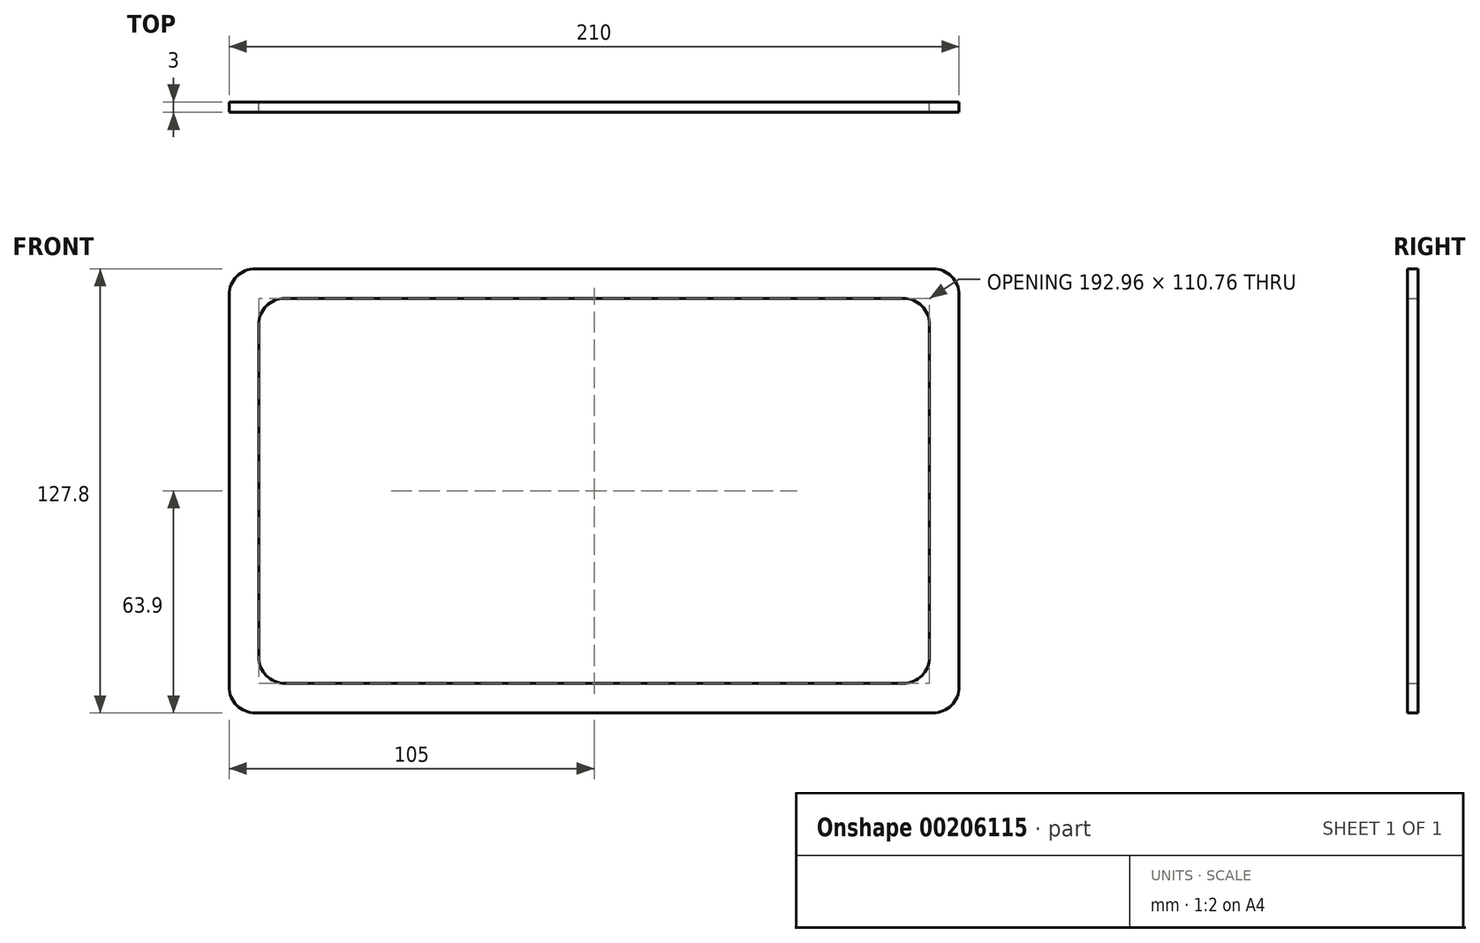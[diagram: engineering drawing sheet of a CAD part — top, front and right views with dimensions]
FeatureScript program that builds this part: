
annotation { "Feature Type Name" : "Feature", "Feature Type Description" : "" }
export const myFeature = defineFeature(function(context is Context, id is Id, definition is map)
    precondition{}
    {
        {
            var Q0;
            Q0=qCreatedBy(makeId("Front.planeOp"),FACE);
            var sketch = newSketch(context, id + "F0", { "sketchPlane" : qUnion([Q0])});
            skLineSegment(sketch, "E0.bottom", {"start": v(96.48, -55.38) * mm, "end": v(-96.48, -55.38) * mm});
            skLineSegment(sketch, "E0.top", {"start": v(96.48, 55.38) * mm, "end": v(-96.48, 55.38) * mm});
            skLineSegment(sketch, "E0.left", {"start": v(96.48, -55.38) * mm, "end": v(96.48, 55.38) * mm});
            skLineSegment(sketch, "E0.right", {"start": v(-96.48, -55.38) * mm, "end": v(-96.48, 55.38) * mm});
            skPoint(sketch, "E0.middle", {"position": v(0, 0) * mm});
            skLineSegment(sketch, "E1.bottom", {"start": v(97.5, 63.9) * mm, "end": v(-97.5, 63.9) * mm});
            skLineSegment(sketch, "E1.top", {"start": v(97.5, -63.9) * mm, "end": v(-97.5, -63.9) * mm});
            skLineSegment(sketch, "E1.left", {"start": v(105, 56.4) * mm, "end": v(105, -56.4) * mm});
            skLineSegment(sketch, "E1.right", {"start": v(-105, 56.4) * mm, "end": v(-105, -56.4) * mm});
            skPoint(sketch, "E2.visualSharp", {"position": v(-105, -63.9) * mm});
            skArc(sketch, "E2.filletArc", {"start": v(-105, -56.4) * mm, "mid": v(-102.8, -61.7) * mm, "end": v(-97.5, -63.9) * mm});
            skPoint(sketch, "E3.visualSharp", {"position": v(105, -63.9) * mm});
            skArc(sketch, "E3.filletArc", {"start": v(97.5, -63.9) * mm, "mid": v(102.8, -61.7) * mm, "end": v(105, -56.4) * mm});
            skPoint(sketch, "E4.visualSharp", {"position": v(105, 63.9) * mm});
            skArc(sketch, "E4.filletArc", {"start": v(105, 56.4) * mm, "mid": v(102.8, 61.7) * mm, "end": v(97.5, 63.9) * mm});
            skPoint(sketch, "E5.visualSharp", {"position": v(-105, 63.9) * mm});
            skArc(sketch, "E5.filletArc", {"start": v(-97.5, 63.9) * mm, "mid": v(-102.8, 61.7) * mm, "end": v(-105, 56.4) * mm});
            skSolve(sketch);
        }
        {
            var Q0;
            Q0=makeQuery(id+"F0.imprint","IMPRINT",FACE,{"disambiguationData":[TD([[makeQuery(id+"F0.imprint","IMPRINT",EDGE,{"derivedFrom":sQuery(id+"F0.wireOp",EDGE,"E0.bottom")}),1.0]])]});
            extrude(context, id + "F1", {"entities" : qUnion([Q0]), "depth" : 3 * mm});
        }
        {
            var Q0;
            Q0=makeQuery(id+"F1.opExtrude","SWEPT_EDGE",EDGE,{"disambiguationData":[OSD([sQuery(id+"F0.wireOp",EDGE,"E0.top"),sQuery(id+"F0.wireOp",EDGE,"E0.left")])]});
            var Q1;
            Q1=makeQuery(id+"F1.opExtrude","SWEPT_EDGE",EDGE,{"disambiguationData":[OSD([sQuery(id+"F0.wireOp",EDGE,"E0.top"),sQuery(id+"F0.wireOp",EDGE,"E0.right")])]});
            var Q2;
            Q2=makeQuery(id+"F1.opExtrude","SWEPT_EDGE",EDGE,{"disambiguationData":[OSD([sQuery(id+"F0.wireOp",EDGE,"E0.bottom"),sQuery(id+"F0.wireOp",EDGE,"E0.right")])]});
            var Q3;
            Q3=makeQuery(id+"F1.opExtrude","SWEPT_EDGE",EDGE,{"disambiguationData":[OSD([sQuery(id+"F0.wireOp",EDGE,"E0.bottom"),sQuery(id+"F0.wireOp",EDGE,"E0.left")])]});
            fillet(context, id + "F2", {"entities" : qUnion([Q0, Q1, Q2, Q3]), "radius" : 7.5 * mm, "tangentPropagation" : true, "allowEdgeOverflow" : false});
        }
    });
